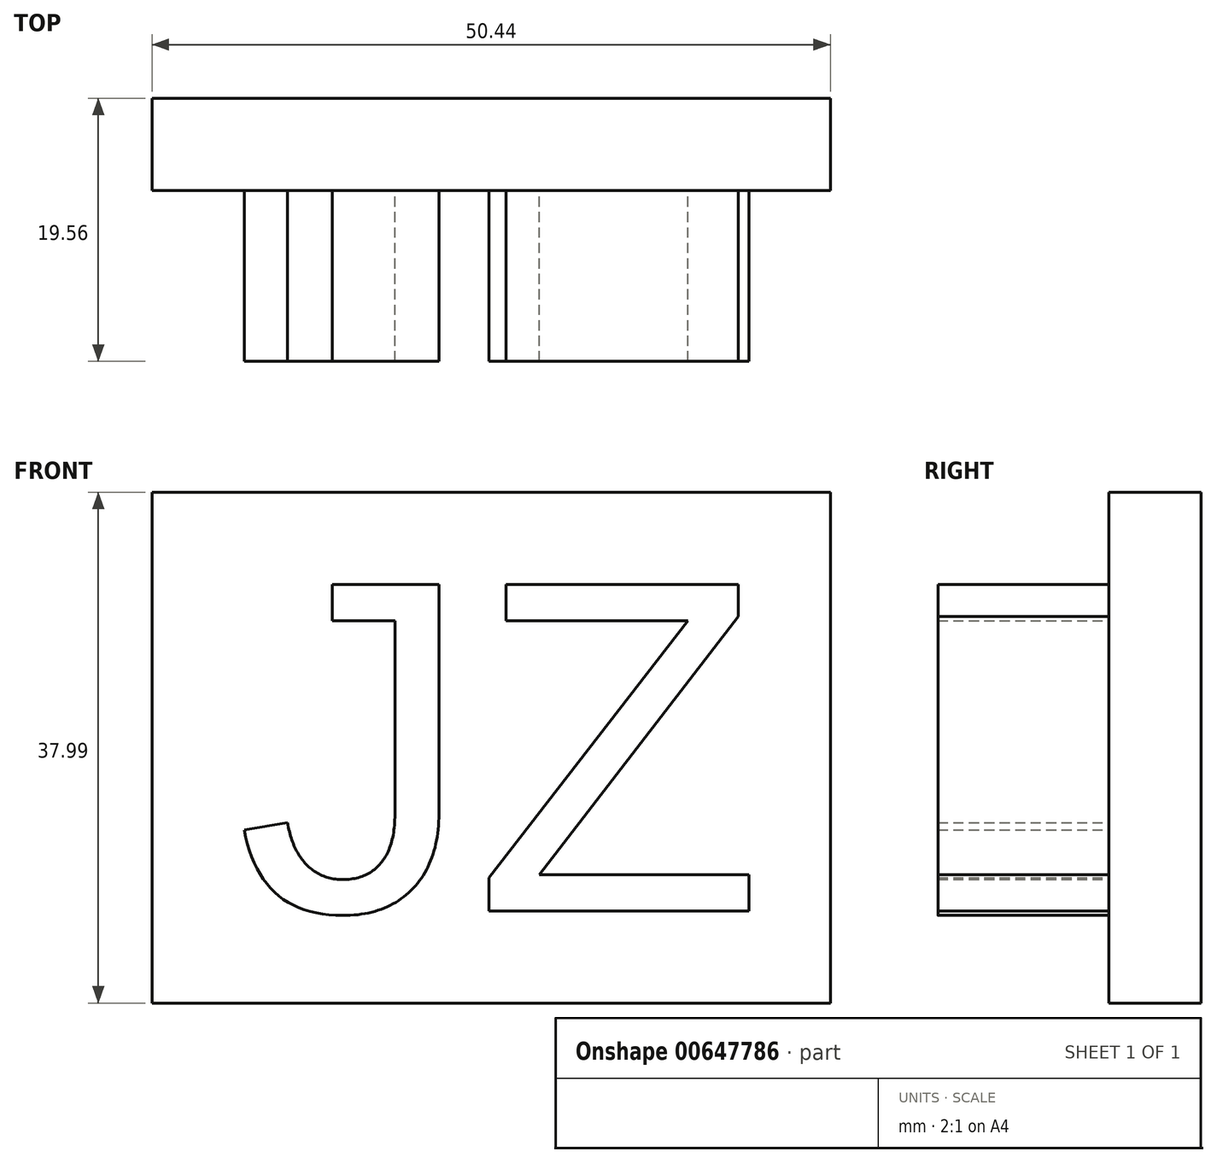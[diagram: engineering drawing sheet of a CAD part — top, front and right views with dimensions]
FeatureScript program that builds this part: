
annotation { "Feature Type Name" : "Feature", "Feature Type Description" : "" }
export const myFeature = defineFeature(function(context is Context, id is Id, definition is map)
    precondition{}
    {
        {
            var Q0;
            Q0=qCreatedBy(makeId("Front.planeOp"),FACE);
            var sketch = newSketch(context, id + "F0", { "sketchPlane" : qUnion([Q0])});
            skText(sketch, "E0", { "text": "JZ\n", "fontName": "Arimo-Regular.ttf"});
            const initialGuessF0  = {"E0": [-0.0181, -0.01214, 1, 0, 0.0254]};
            skSetInitialGuess(sketch, initialGuessF0);
            skSolve(sketch);
        }
        {
            var Q0;
            Q0=qSketchRegion(id+"F0",true);
            extrude(context, id + "F1", {"entities" : qUnion([Q0]), "depth" : 12.7 * mm, "offsetDistance" : 25.4 * mm});
        }
        {
            var Q0;
            Q0=qCreatedBy(makeId("Front.planeOp"),FACE);
            var sketch = newSketch(context, id + "F2", { "sketchPlane" : qUnion([Q0])});
            skLineSegment(sketch, "E1.bottom", {"start": v(-24.41, 18.99) * mm, "end": v(26.03, 18.99) * mm});
            skLineSegment(sketch, "E1.top", {"start": v(-24.41, -19) * mm, "end": v(26.03, -19) * mm});
            skLineSegment(sketch, "E1.left", {"start": v(-24.41, 18.99) * mm, "end": v(-24.41, -19) * mm});
            skLineSegment(sketch, "E1.right", {"start": v(26.03, 18.99) * mm, "end": v(26.03, -19) * mm});
            skSolve(sketch);
        }
        {
            var Q0;
            Q0=qSketchRegion(id+"F2",true);
            extrude(context, id + "F3", {"entities" : qUnion([Q0]), "operationType" : NewBodyOperationType.ADD, "oppositeDirection" : true, "depth" : 6.86 * mm, "offsetDistance" : 25.4 * mm});
        }
    });
